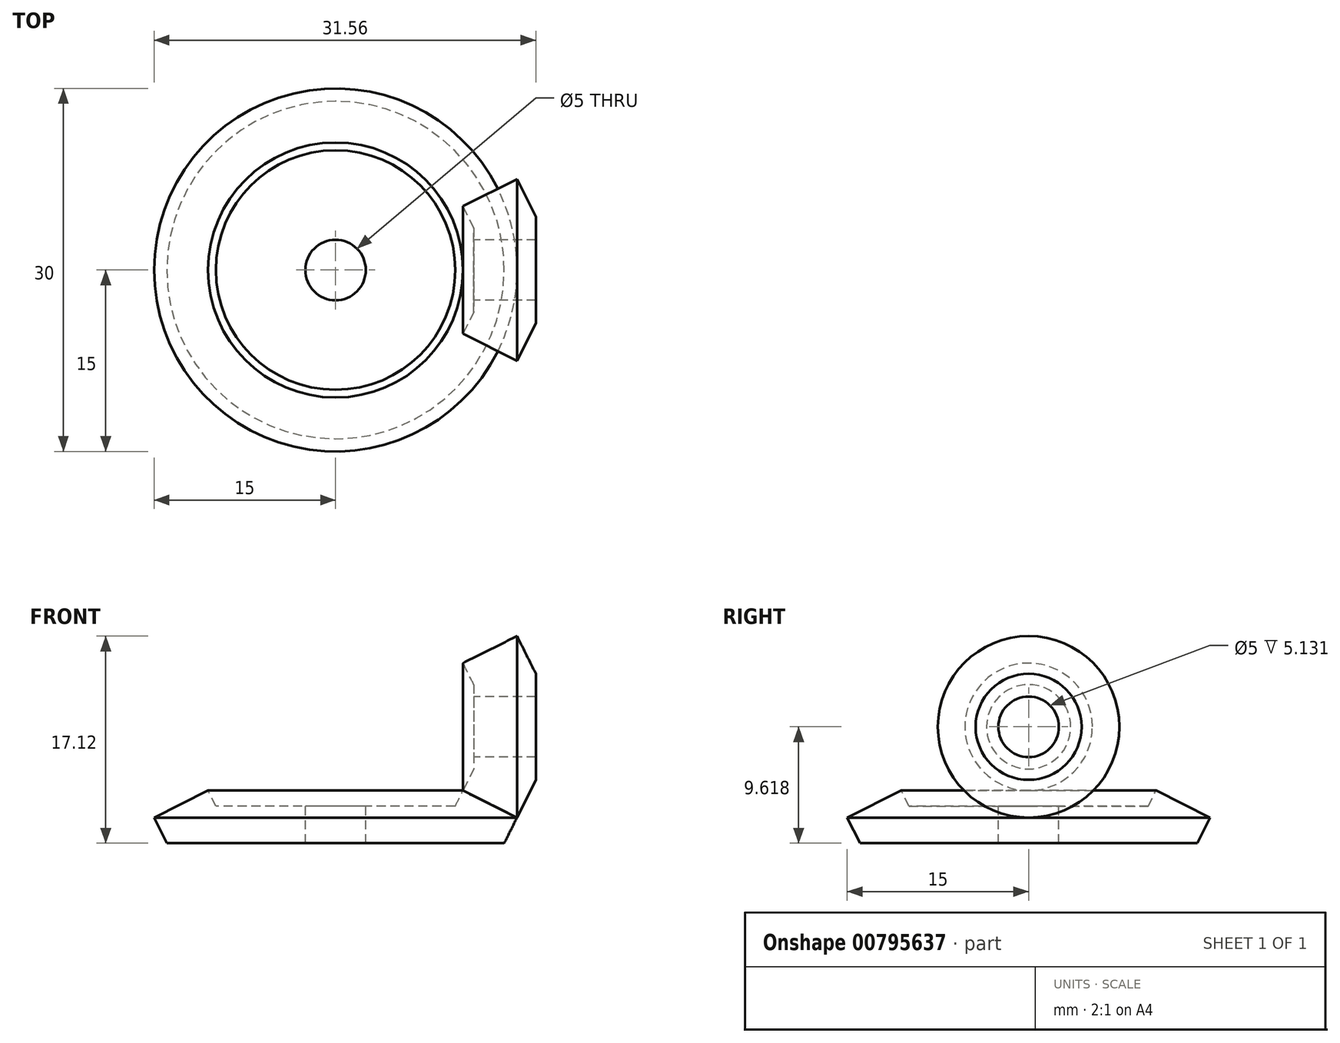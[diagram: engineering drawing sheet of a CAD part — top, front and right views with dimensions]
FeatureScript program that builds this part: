
annotation { "Feature Type Name" : "Feature", "Feature Type Description" : "" }
export const myFeature = defineFeature(function(context is Context, id is Id, definition is map)
    precondition{}
    {
        {
            var Q0;
            Q0=qCreatedBy(makeId("Front.planeOp"),FACE);
            var sketch = newSketch(context, id + "F0", { "sketchPlane" : qUnion([Q0])});
            skLineSegment(sketch, "E0", {"start": v(0, 12.83) * mm, "end": v(0, -6.69) * mm, "construction": true});
            skLineSegment(sketch, "E1", {"start": v(0, 8.62) * mm, "end": v(16.9, 0.17) * mm, "construction": true});
            skLineSegment(sketch, "E2", {"start": v(0, -1) * mm, "end": v(13.94, -1) * mm});
            skLineSegment(sketch, "E3", {"start": v(13.94, -1) * mm, "end": v(15.45, 2.01) * mm});
            skLineSegment(sketch, "E4", {"start": v(15.45, 2.01) * mm, "end": v(10.85, 3.98) * mm});
            skLineSegment(sketch, "E5", {"start": v(10.85, 3.98) * mm, "end": v(9.9, 2.06) * mm});
            skLineSegment(sketch, "E6", {"start": v(9.9, 2.06) * mm, "end": v(0, 2.06) * mm});
            skPoint(sketch, "E7", {"position": v(14.44, 0) * mm});
            skPoint(sketch, "E8", {"position": v(15, 1.12) * mm});
            skPoint(sketch, "E9", {"position": v(10.14, 2.56) * mm});
            skLineSegment(sketch, "E10", {"start": v(0, 8.62) * mm, "end": v(17.46, 1.15) * mm, "construction": true});
            skLineSegment(sketch, "E11", {"start": v(0, 8.62) * mm, "end": v(16.3, -1.1) * mm, "construction": true});
            skPoint(sketch, "E12", {"position": v(10.54, 3.35) * mm});
            skLineSegment(sketch, "E13", {"start": v(0, 2.06) * mm, "end": v(0, -1) * mm});
            skLineSegment(sketch, "E14", {"start": v(2.5, 2.06) * mm, "end": v(2.5, -1) * mm});
            skSolve(sketch);
        }
        {
            var Q0;
            Q0=qCreatedBy(makeId("Front.planeOp"),FACE);
            var sketch = newSketch(context, id + "F1", { "sketchPlane" : qUnion([Q0])});
            skLineSegment(sketch, "E15.0", {"start": v(9.9, 2.06) * mm, "end": v(2.5, 2.06) * mm});
            skLineSegment(sketch, "E16.0", {"start": v(10.54, 3.35) * mm, "end": v(9.9, 2.06) * mm});
            skLineSegment(sketch, "E17.0", {"start": v(10.54, 3.35) * mm, "end": v(15, 1.12) * mm});
            skLineSegment(sketch, "E18.0", {"start": v(13.94, -1) * mm, "end": v(15, 1.12) * mm});
            skLineSegment(sketch, "E19.0", {"start": v(2.5, -1) * mm, "end": v(13.94, -1) * mm});
            skLineSegment(sketch, "E20.0", {"start": v(2.5, 2.06) * mm, "end": v(2.5, -1) * mm});
            skSolve(sketch);
        }
        {
            var Q0;
            Q0=qSketchRegion(id+"F1",true);
            var Q1;
            Q1=sQuery(id+"F0.wireOp",EDGE,"E0");
            revolve(context, id + "F2", {"entities" : qUnion([Q0]), "axis" : qUnion([Q1]), "revolveType" : RevolveType.FULL});
        }
        {
            var Q0;
            Q0=qCreatedBy(makeId("Front.planeOp"),FACE);
            var sketch = newSketch(context, id + "F3", { "sketchPlane" : qUnion([Q0])});
            skLineSegment(sketch, "E21", {"start": v(-2.32, 8.62) * mm, "end": v(21.4, 8.62) * mm, "construction": true});
            skLineSegment(sketch, "E22", {"start": v(11.43, 8.62) * mm, "end": v(16.56, 8.62) * mm});
            skLineSegment(sketch, "E23.MirrorCS", {"start": v(10.22, 2.72) * mm, "end": v(11.43, 5.14) * mm});
            skLineSegment(sketch, "E24.MirrorCS", {"start": v(14.55, 0.22) * mm, "end": v(10.22, 2.72) * mm});
            skPoint(sketch, "E25.MirrorP", {"position": v(15, 1.12) * mm});
            skPoint(sketch, "E26.MirrorP", {"position": v(10.93, 4.14) * mm});
            skPoint(sketch, "E27.MirrorP", {"position": v(10.54, 3.35) * mm});
            skLineSegment(sketch, "E28.MirrorCS", {"start": v(11.43, 6.12) * mm, "end": v(16.56, 6.12) * mm});
            skPoint(sketch, "E29.MirrorP", {"position": v(15.56, 2.24) * mm});
            skLineSegment(sketch, "E30.MirrorCS", {"start": v(0, 8.62) * mm, "end": v(17.57, 1.41) * mm, "construction": true});
            skLineSegment(sketch, "E31.MirrorCS", {"start": v(0, 8.62) * mm, "end": v(17.24, 0) * mm, "construction": true});
            skLineSegment(sketch, "E32.MirrorCS", {"start": v(0, 8.62) * mm, "end": v(16.4, -0.85) * mm, "construction": true});
            skLineSegment(sketch, "E33.MirrorCS", {"start": v(11.43, 5.14) * mm, "end": v(11.43, 8.62) * mm});
            skLineSegment(sketch, "E34.MirrorCS", {"start": v(16.56, 4.24) * mm, "end": v(14.55, 0.22) * mm});
            skLineSegment(sketch, "E35.MirrorCS", {"start": v(16.56, 8.62) * mm, "end": v(16.56, 4.24) * mm});
            skSolve(sketch);
        }
        {
            var Q0;
            Q0=qCreatedBy(makeId("Front.planeOp"),FACE);
            var sketch = newSketch(context, id + "F4", { "sketchPlane" : qUnion([Q0])});
            skLineSegment(sketch, "E36.0", {"start": v(11.43, 5.14) * mm, "end": v(11.43, 6.12) * mm});
            skLineSegment(sketch, "E37.0", {"start": v(11.43, 6.12) * mm, "end": v(16.56, 6.12) * mm});
            skLineSegment(sketch, "E38.0", {"start": v(16.56, 6.12) * mm, "end": v(16.56, 4.24) * mm});
            skLineSegment(sketch, "E39.0", {"start": v(16.56, 4.24) * mm, "end": v(15, 1.12) * mm});
            skLineSegment(sketch, "E40.0", {"start": v(10.54, 3.35) * mm, "end": v(15, 1.12) * mm});
            skLineSegment(sketch, "E41.0", {"start": v(10.54, 3.35) * mm, "end": v(11.43, 5.14) * mm});
            skSolve(sketch);
        }
        {
            var Q0;
            Q0=qSketchRegion(id+"F4",true);
            var Q1;
            Q1=sQuery(id+"F3.wireOp",EDGE,"E21");
            revolve(context, id + "F5", {"operationType" : NewBodyOperationType.ADD, "entities" : qUnion([Q0]), "axis" : qUnion([Q1]), "revolveType" : RevolveType.FULL});
        }
    });
